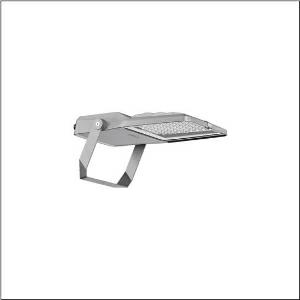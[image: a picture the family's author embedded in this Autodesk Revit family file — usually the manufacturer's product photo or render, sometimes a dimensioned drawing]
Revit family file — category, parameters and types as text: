
# Revit family: floodlight_fl_21_iq_mini___pl33t_5xa7772b3f1a_8999
name_source: partatom
category: Lighting Fixtures
units: mm (PartAtom-declared; Revit-internal decimal feet)

## family parameters
Cut with Voids When Loaded = No
Host = Face
Light Source = No
Part Type = Normal
Room Calculation Point = No
Round Connector Dimension = Use Diameter
Shared = No

## types (1)
- --- (1 x LED, 5310 lm, 45.5 W, 3000K)
    Apparent Load = 46 VA
    CIE Flux Codes = 26 75 99 100 100
    Color Rendering = 80
    Color Temperature = 3000K
    Default Elevation = 1800 mm
    Description = Floodlight FL 21 iQ mini, floodlight, primary light control with lens, of PMMA, primary optical cover: protective disc, of toughened safety glass, transparent, light distribution: PL33T, light emission: direct distribution, installation type: surface-mounted, lamps: LED, High Power LED, rated values: 5.310lm | 45,5W | 116,7lm/W (begin service life); end service life: 5.310lm | 48W; at 50% lumin. flux: 2.655lm | 21,4W | 124,1lm/W, colour temperature: 3000K, colour rendering: CRI > 80, light colour: 830, light setting 1 begin service life: 100% | 5.310lm | 45,5W | 116,7lm/W | 3.000K, light setting 1 end service life: 48W, further light settings possible, control: Street-Remote, Auto-Match, Temp-Guard, Night-Set, Smart-Wire, Desk-Remote (wireless, voltage-free reading and setting of iQ features in the workshop via application-optimized NFC function/RFID function), optimised constant luminous flux control (CLO 2.0), pre-setting: linear dimming characteristic, with terminal, 6-pole, mains connection: 220..240V, AC, 50/60Hz, luminaire housing, of diecast aluminium, powder-coated, SITECO metallic grey (DB 702S), corrosivity category C5 mid according to DIN EN ISO 12944suitable for swimming poolschlorine-resistant, sealing non-destructively replaceable, mounting bracket, of steel, galvanised, powder-coated, SITECO metallic grey (DB 702S), protection rating (complete): IP66, insulation class (complete): insulation class II (safety insulation), certification: CE, ENEC, VDE, protection symbol: D, impact resistance: IK08, permissible operating ambient temperature: -40..+40°C, permissible operating ambient temperature for outdoor applications: -40..+50°C, standard: DIN EN 12944, LABS conformity tested according to VDMA 24364:2018-05, packaging unit: 1 piece

Light Distribution: PL33T
    Height = 70 mm
    Lamp = 1 x LED
    Lamp Light Flux = 5310 lm
    Lamp Power = 45.5 W
    Lamp count = 1
    Length = 485 mm
    Luminous efficacy = 117 lm/W
    Manufacturer = Siteco
    ModVariant = No
    Model = 5XA7772B3F1A
    Number of Poles = 1
    OnlyDefault = Yes
    Power Factor = 1
    Product Name = Floodlight FL 21 iQ mini | PL33T
    Product group = floodlight | pylon annexe
    ProductGroupID = 6201
    Protection Class = Protection class II
    Protection Degree = IP 66
    RLX_Detail_Level = 1
    RLX_Emergency_Light_Flux = 0 lm
    RLX_Emergency_Type = 0
    RLX_Emergency_Type_DB = No
    RlxData = <blob elided: 96317 chars, md5=4423a7cc>
    Socket = socket
    Standby Power = 0 W
    System Light Flux = 5310 lm
    System Power = 46 W
    Type Comments = factory setting: luminous flux: 100 % | dim-lin: 254 | 463 mA
    Type Image = l_1006845.jpg
    URL = http://relux.com
    VarID = @adj_149491
    Voltage = 0 V
    Weight = 0.00 kg
    Width = 337 mm

## geometry (parser evidence)
native form markers: Blend x4, Sweep x15
no freeform markers — native parametric forms only
